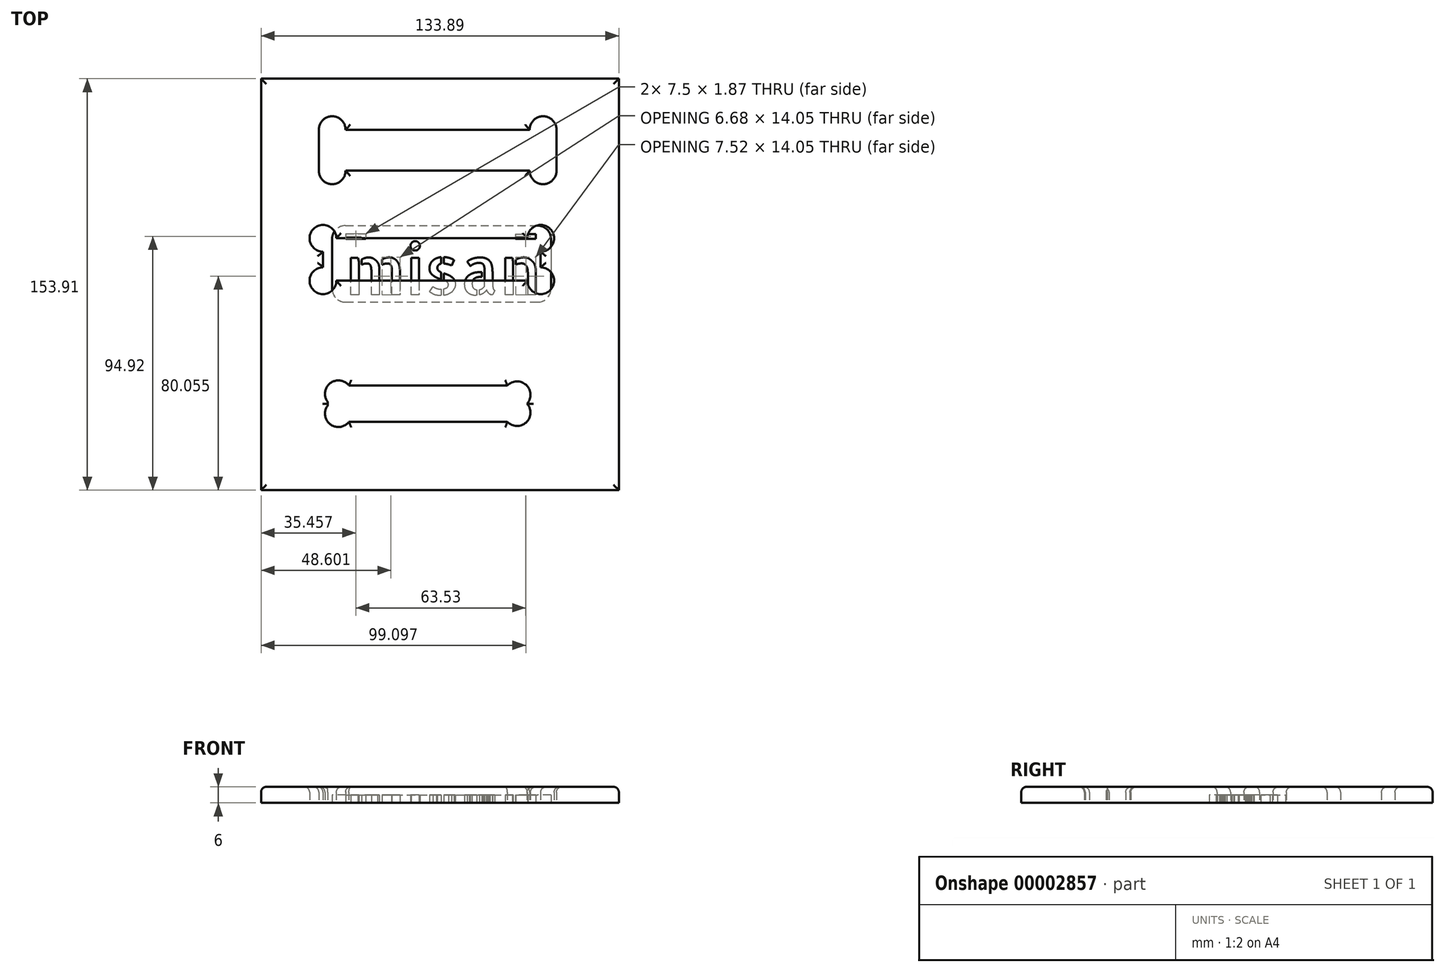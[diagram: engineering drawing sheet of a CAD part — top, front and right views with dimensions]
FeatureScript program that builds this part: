
annotation { "Feature Type Name" : "Feature", "Feature Type Description" : "" }
export const myFeature = defineFeature(function(context is Context, id is Id, definition is map)
    precondition{}
    {
        {
            var Q0;
            Q0=qCreatedBy(makeId("Top.planeOp"),FACE);
            var sketch = newSketch(context, id + "F0", { "sketchPlane" : qUnion([Q0])});
            skLineSegment(sketch, "E0.rect.top", {"start": v(-40.74, -7.94) * mm, "end": v(-40.74, -7.94) * mm});
            skPoint(sketch, "E0.rect.middle", {"position": v(0, 0) * mm});
            skLineSegment(sketch, "E1", {"start": v(-35.74, 7.94) * mm, "end": v(35.74, 7.94) * mm});
            skArc(sketch, "E2", {"start": v(-40.74, -2.94) * mm, "mid": v(-44.27, -11.47) * mm, "end": v(-35.74, -7.94) * mm});
            skArc(sketch, "E3", {"start": v(35.74, -7.94) * mm, "mid": v(44.27, -11.47) * mm, "end": v(40.74, -2.94) * mm});
            skLineSegment(sketch, "E4", {"start": v(40.74, 2.94) * mm, "end": v(40.74, -2.94) * mm});
            skArc(sketch, "E5", {"start": v(-35.74, 7.94) * mm, "mid": v(-44.27, 11.47) * mm, "end": v(-40.74, 2.94) * mm});
            skLineSegment(sketch, "E6", {"start": v(-40.74, 2.94) * mm, "end": v(-40.74, -2.94) * mm});
            skLineSegment(sketch, "E7", {"start": v(-35.74, -7.94) * mm, "end": v(35.74, -7.94) * mm});
            skArc(sketch, "E8", {"start": v(40.74, 2.94) * mm, "mid": v(44.27, 11.47) * mm, "end": v(35.74, 7.94) * mm});
            skArc(sketch, "E9", {"start": v(40.74, -2.94) * mm, "mid": v(40.74, -12.94) * mm, "end": v(40.74, -2.94) * mm});
            skLineSegment(sketch, "E10", {"start": v(40.74, -7.94) * mm, "end": v(40.74, -7.94) * mm});
            skLineSegment(sketch, "E11", {"start": v(40.74, -7.7) * mm, "end": v(40.74, -7.94) * mm});
            skLineSegment(sketch, "E12.left", {"start": v(-42.28, 48.54) * mm, "end": v(-42.28, 33.2) * mm});
            skLineSegment(sketch, "E12.right", {"start": v(46.62, 48.54) * mm, "end": v(46.62, 33.2) * mm});
            skPoint(sketch, "E13.second.point", {"position": v(-32.98, -54.82) * mm});
            skPoint(sketch, "E13.third.point", {"position": v(-30.61, -52.65) * mm});
            skPoint(sketch, "E14.second.point", {"position": v(-37.89, -53.58) * mm});
            skPoint(sketch, "E14.third.point", {"position": v(-31.06, -60.74) * mm});
            skPoint(sketch, "E15.second.point", {"position": v(28.27, -60.74) * mm});
            skPoint(sketch, "E16.second.point", {"position": v(32.87, -55.5) * mm});
            skPoint(sketch, "E16.third.point", {"position": v(27.57, -53.13) * mm});
            skLineSegment(sketch, "E17", {"start": v(-31.06, -47.15) * mm, "end": v(28.27, -47.15) * mm});
            skArc(sketch, "E18", {"start": v(-31.06, -47.15) * mm, "mid": v(-38.08, -46.3) * mm, "end": v(-38.92, -53.32) * mm});
            skLineSegment(sketch, "E19", {"start": v(-38.92, -53.32) * mm, "end": v(-38.92, -54.56) * mm});
            skArc(sketch, "E20", {"start": v(-38.92, -54.56) * mm, "mid": v(-38.08, -61.58) * mm, "end": v(-31.06, -60.74) * mm});
            skLineSegment(sketch, "E21", {"start": v(-31.06, -60.74) * mm, "end": v(28.27, -60.74) * mm});
            skArc(sketch, "E22", {"start": v(28.27, -60.74) * mm, "mid": v(35.28, -60.95) * mm, "end": v(35.6, -53.94) * mm});
            skArc(sketch, "E23", {"start": v(35.6, -53.94) * mm, "mid": v(35.28, -46.94) * mm, "end": v(28.27, -47.15) * mm});
            skPoint(sketch, "E24.second.point", {"position": v(-32.28, 48.54) * mm});
            skPoint(sketch, "E24.third.point", {"position": v(-35.86, 53.36) * mm});
            skPoint(sketch, "E25.second.point", {"position": v(-32.28, 33.2) * mm});
            skPoint(sketch, "E25.third.point", {"position": v(-35.86, 28.39) * mm});
            skPoint(sketch, "E26.second.point", {"position": v(36.62, 48.54) * mm});
            skPoint(sketch, "E26.third.point", {"position": v(41.5, 53.56) * mm});
            skPoint(sketch, "E27.second.point", {"position": v(36.62, 33.2) * mm});
            skPoint(sketch, "E27.third.point", {"position": v(41.5, 28.19) * mm});
            skLineSegment(sketch, "E28", {"start": v(-32.28, 48.54) * mm, "end": v(36.62, 48.54) * mm});
            skArc(sketch, "E29", {"start": v(-32.28, 48.54) * mm, "mid": v(-37.28, 53.56) * mm, "end": v(-42.28, 48.54) * mm});
            skLineSegment(sketch, "E30", {"start": v(-32.28, 33.2) * mm, "end": v(36.62, 33.2) * mm});
            skArc(sketch, "E31", {"start": v(-42.28, 33.2) * mm, "mid": v(-37.28, 28.18) * mm, "end": v(-32.28, 33.2) * mm});
            skLineSegment(sketch, "E32", {"start": v(46.62, 33.2) * mm, "end": v(46.62, 33.2) * mm});
            skArc(sketch, "E33", {"start": v(36.62, 33.2) * mm, "mid": v(41.62, 28.18) * mm, "end": v(46.62, 33.2) * mm});
            skArc(sketch, "E34", {"start": v(46.62, 48.54) * mm, "mid": v(41.62, 53.56) * mm, "end": v(36.62, 48.54) * mm});
            skLineSegment(sketch, "E35", {"start": v(46.62, 48.54) * mm, "end": v(46.62, 48.54) * mm});
            skLineSegment(sketch, "E36.bottom", {"start": v(-63.9, 67.65) * mm, "end": v(69.98, 67.65) * mm});
            skLineSegment(sketch, "E36.top", {"start": v(-63.9, -86.26) * mm, "end": v(69.98, -86.26) * mm});
            skLineSegment(sketch, "E36.left", {"start": v(-63.9, 67.65) * mm, "end": v(-63.9, -86.26) * mm});
            skLineSegment(sketch, "E36.right", {"start": v(69.98, 67.65) * mm, "end": v(69.98, -86.26) * mm});
            skSolve(sketch);
        }
        {
            var Q0;
            Q0=makeQuery(id+"F0.imprint","IMPRINT",FACE,{"disambiguationData":[TD([[makeQuery(id+"F0.imprint","IMPRINT",EDGE,{"derivedFrom":sQuery(id+"F0.wireOp",EDGE,"E1")}),1.0]])]});
            extrude(context, id + "F1", {"entities" : qUnion([Q0]), "depth" : 6 * mm});
        }
        {
            var Q0;
            Q0=makeQuery(id+"F1.opExtrude","CAP_FACE",FACE,{"disambiguationData":[OSD([sQuery(id+"F0.wireOp",EDGE,"E1"),sQuery(id+"F0.wireOp",EDGE,"E2"),sQuery(id+"F0.wireOp",EDGE,"E3"),sQuery(id+"F0.wireOp",EDGE,"E4"),sQuery(id+"F0.wireOp",EDGE,"E5"),sQuery(id+"F0.wireOp",EDGE,"E6"),sQuery(id+"F0.wireOp",EDGE,"E7"),sQuery(id+"F0.wireOp",EDGE,"E8"),sQuery(id+"F0.wireOp",EDGE,"E12.left"),sQuery(id+"F0.wireOp",EDGE,"E12.right"),sQuery(id+"F0.wireOp",EDGE,"E17"),sQuery(id+"F0.wireOp",EDGE,"E18"),sQuery(id+"F0.wireOp",EDGE,"E19"),sQuery(id+"F0.wireOp",EDGE,"E20"),sQuery(id+"F0.wireOp",EDGE,"E21"),sQuery(id+"F0.wireOp",EDGE,"E22"),sQuery(id+"F0.wireOp",EDGE,"E23"),sQuery(id+"F0.wireOp",EDGE,"E28"),sQuery(id+"F0.wireOp",EDGE,"E29"),sQuery(id+"F0.wireOp",EDGE,"E30"),sQuery(id+"F0.wireOp",EDGE,"E31"),sQuery(id+"F0.wireOp",EDGE,"E33"),sQuery(id+"F0.wireOp",EDGE,"E34"),sQuery(id+"F0.wireOp",EDGE,"E36.bottom"),sQuery(id+"F0.wireOp",EDGE,"E36.top"),sQuery(id+"F0.wireOp",EDGE,"E36.left"),sQuery(id+"F0.wireOp",EDGE,"E36.right")])],"isStart":false});
            fillet(context, id + "F2", {"entities" : qUnion([Q0]), "radius" : 2 * mm, "tangentPropagation" : true, "allowEdgeOverflow" : false});
        }
        {
            var Q0;
            Q0=qCreatedBy(makeId("Top.planeOp"),FACE);
            var sketch = newSketch(context, id + "F3", { "sketchPlane" : qUnion([Q0])});
            skLineSegment(sketch, "E37.bottom", {"start": v(-32.31, 12.7) * mm, "end": v(39.56, 12.7) * mm});
            skLineSegment(sketch, "E37.top", {"start": v(-32.31, -15.95) * mm, "end": v(39.56, -15.95) * mm});
            skLineSegment(sketch, "E37.left", {"start": v(-37.31, 7.7) * mm, "end": v(-37.31, -10.95) * mm});
            skLineSegment(sketch, "E37.right", {"start": v(44.56, 7.7) * mm, "end": v(44.56, -10.95) * mm});
            skPoint(sketch, "E38.visualSharp", {"position": v(-37.31, 12.7) * mm});
            skArc(sketch, "E38.filletArc", {"start": v(-32.31, 12.7) * mm, "mid": v(-35.85, 11.23) * mm, "end": v(-37.31, 7.7) * mm});
            skPoint(sketch, "E39.visualSharp", {"position": v(44.56, 12.7) * mm});
            skArc(sketch, "E39.filletArc", {"start": v(44.56, 7.7) * mm, "mid": v(43.1, 11.23) * mm, "end": v(39.56, 12.7) * mm});
            skPoint(sketch, "E40.visualSharp", {"position": v(44.56, -15.95) * mm});
            skArc(sketch, "E40.filletArc", {"start": v(39.56, -15.95) * mm, "mid": v(43.1, -14.48) * mm, "end": v(44.56, -10.95) * mm});
            skPoint(sketch, "E41.visualSharp", {"position": v(-37.31, -15.95) * mm});
            skArc(sketch, "E41.filletArc", {"start": v(-37.31, -10.95) * mm, "mid": v(-35.85, -14.48) * mm, "end": v(-32.31, -15.95) * mm});
            skText(sketch, "E42", { "text": "misan", "fontName": "AllertaStencil-Regular.ttf"});
            skLineSegment(sketch, "E43.bottom", {"start": v(-32.2, 9.6) * mm, "end": v(-24.7, 9.6) * mm});
            skLineSegment(sketch, "E43.top", {"start": v(-32.2, 7.73) * mm, "end": v(-24.7, 7.73) * mm});
            skLineSegment(sketch, "E43.left", {"start": v(-32.2, 9.6) * mm, "end": v(-32.2, 7.73) * mm});
            skLineSegment(sketch, "E43.right", {"start": v(-24.7, 9.6) * mm, "end": v(-24.7, 7.73) * mm});
            skLineSegment(sketch, "E44.bottom", {"start": v(31.33, 9.57) * mm, "end": v(38.83, 9.57) * mm});
            skLineSegment(sketch, "E44.top", {"start": v(31.33, 7.7) * mm, "end": v(38.83, 7.7) * mm});
            skLineSegment(sketch, "E44.left", {"start": v(31.33, 9.57) * mm, "end": v(31.33, 7.7) * mm});
            skLineSegment(sketch, "E44.right", {"start": v(38.83, 9.57) * mm, "end": v(38.83, 7.7) * mm});
            const initialGuessF3  = {"E42": [-0.03245, -0.01323, 1, 0, 0.01817]};
            skSetInitialGuess(sketch, initialGuessF3);
            skSolve(sketch);
        }
        {
            var Q0;
            Q0=makeQuery(id+"F3.imprint","IMPRINT",FACE,{"disambiguationData":[TD([[makeQuery(id+"F3.imprint","IMPRINT",EDGE,{"derivedFrom":sQuery(id+"F3.wireOp",EDGE,"E37.bottom")}),-1.0]])]});
            extrude(context, id + "F4", {"entities" : qUnion([Q0]), "depth" : 3 * mm});
        }
    });
